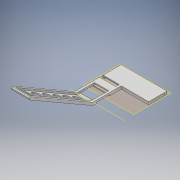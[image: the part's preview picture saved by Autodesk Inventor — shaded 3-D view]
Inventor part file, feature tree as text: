
AUTODESK INVENTOR PART (.ipt)
format: ipt  version: 2018 (Build 220112000, 112)  size: 257,024 bytes
history: native  units: mm
features: extrude x8, sketch x5, other x2, plane x2, mirror x2
ambient origin geometry x8: Origin, YZ Plane, XZ Plane, XY Plane, X Axis, Y Axis, Z Axis, Center Point
bodies: Body1 (feature_tree)
feature tree (19):
  other  "Sólido1"
  sketch  "Boceto1"  dims[d7=5.0mm d9=2.5mm d10=0.0mm]
  extrude  "Extrusión1"  Depth=2.5mm TaperAngle=0.0deg
  extrude  "Extrusión2"  Depth=5.0mm
  plane  "Plano de trabajo3"
  mirror  "Simetría3"
  extrude  "Extrusión11"  Depth=5.0mm
  sketch  "Boceto7"  dims[d69=33.5mm d74=5.0mm]
  plane  "Plano de trabajo4"
  extrude  "Extrusión12"  Depth=5.0mm
  extrude  "Extrusión13"  Depth=8.0mm
  extrude  "Extrusión14"  Depth=4.5mm TaperAngle=0.0deg
  mirror  "Simetría4"
  extrude  "Extrusión15"  Depth=31.5mm
  sketch  "Boceto9"  dims[d77=70.0mm d78=8.0mm d79=4.5mm d80=0.0mm d81=42.4mm d82=173.0mm d86=21.75mm d87=0.0mm d88=120.0deg d89=5.0mm d90=0.0mm d92=21.75mm d93=0.0mm d94=5.0mm d95=20.5mm d96=5.0mm d97=5.0mm d98=5.0mm d99=5.0mm d100=5.0mm d101=22.0mm d102=22.38mm d103=23.0mm d104=24.38mm d105=25.5mm d106=21.75mm d107=0.0mm d108=5.0mm d109=2.5mm d110=40.0mm d111=30.0mm d112=31.5mm d113=21.75mm d114=0.0mm]
  other  "Eje de trabajo2"
  extrude  "Extrusión16"  Depth=31.5mm
  sketch  "Boceto6"  dims[d11=1.0mm d12=0.0mm d68=5.0mm]
  sketch  "Boceto8"  dims[d75=33.5mm d76=5.0mm]
